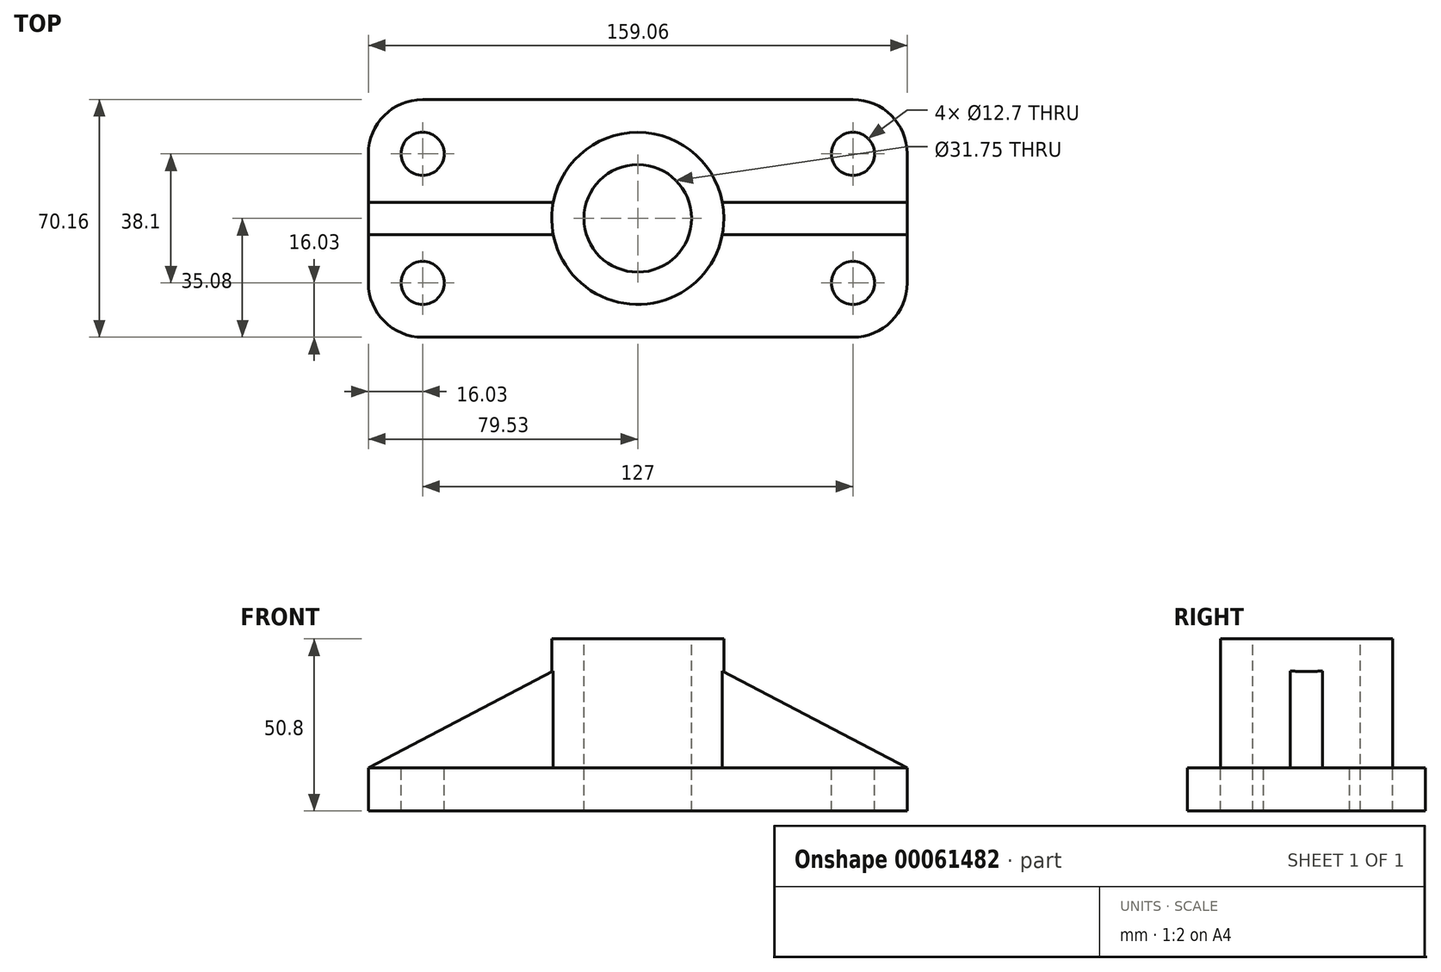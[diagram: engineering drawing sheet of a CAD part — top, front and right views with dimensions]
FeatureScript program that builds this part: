
annotation { "Feature Type Name" : "Feature", "Feature Type Description" : "" }
export const myFeature = defineFeature(function(context is Context, id is Id, definition is map)
    precondition{}
    {
        {
            var Q0;
            Q0=qCreatedBy(makeId("Top.planeOp"),FACE);
            var sketch = newSketch(context, id + "F0", { "sketchPlane" : qUnion([Q0])});
            skLineSegment(sketch, "E0", {"start": v(0, 19.05) * mm, "end": v(0, 0) * mm, "construction": true});
            skLineSegment(sketch, "E1", {"start": v(0, 0) * mm, "end": v(63.5, 0) * mm, "construction": true});
            skLineSegment(sketch, "E2", {"start": v(63.5, 0) * mm, "end": v(63.5, 19.05) * mm, "construction": true});
            skCircle(sketch, "E3", {"center": v(63.5, 19.05) * mm, "radius": 6.35 * mm});
            skCircle(sketch, "E4.MirrorC", {"center": v(63.5, -19.05) * mm, "radius": 6.35 * mm});
            skCircle(sketch, "E5.MirrorC", {"center": v(-63.5, 19.05) * mm, "radius": 6.35 * mm});
            skCircle(sketch, "E6.MirrorC", {"center": v(-63.5, -19.05) * mm, "radius": 6.35 * mm});
            skLineSegment(sketch, "E7", {"start": v(0, -35.08) * mm, "end": v(63.5, -35.08) * mm});
            skLineSegment(sketch, "E8", {"start": v(79.53, 0) * mm, "end": v(79.53, -19.05) * mm});
            skArc(sketch, "E9", {"start": v(63.5, -35.08) * mm, "mid": v(74.83, -30.38) * mm, "end": v(79.53, -19.05) * mm});
            skLineSegment(sketch, "E10.MirrorCS", {"start": v(79.53, 0) * mm, "end": v(79.53, 19.05) * mm});
            skArc(sketch, "E11.MirrorCS", {"start": v(63.5, 35.08) * mm, "mid": v(74.83, 30.38) * mm, "end": v(79.53, 19.05) * mm});
            skLineSegment(sketch, "E12.MirrorCS", {"start": v(0, 35.08) * mm, "end": v(63.5, 35.08) * mm});
            skLineSegment(sketch, "E13.MirrorCS", {"start": v(0, 35.08) * mm, "end": v(-63.5, 35.08) * mm});
            skArc(sketch, "E14.MirrorCS", {"start": v(-63.5, 35.08) * mm, "mid": v(-74.83, 30.38) * mm, "end": v(-79.53, 19.05) * mm});
            skLineSegment(sketch, "E15.MirrorCS", {"start": v(-79.53, 0) * mm, "end": v(-79.53, 19.05) * mm});
            skLineSegment(sketch, "E16.MirrorCS", {"start": v(-79.53, 0) * mm, "end": v(-79.53, -19.05) * mm});
            skArc(sketch, "E17.MirrorCS", {"start": v(-63.5, -35.08) * mm, "mid": v(-74.83, -30.38) * mm, "end": v(-79.53, -19.05) * mm});
            skLineSegment(sketch, "E18.MirrorCS", {"start": v(0, -35.08) * mm, "end": v(-63.5, -35.08) * mm});
            skSolve(sketch);
        }
        {
            var Q0;
            Q0=makeQuery(id+"F0.imprint","IMPRINT",FACE,{"disambiguationData":[TD([[makeQuery(id+"F0.imprint","IMPRINT",EDGE,{"derivedFrom":sQuery(id+"F0.wireOp",EDGE,"E3")}),-1.0]])]});
            extrude(context, id + "F1", {"entities" : qUnion([Q0]), "oppositeDirection" : true, "depth" : 12.7 * mm});
        }
        {
            var Q0;
            Q0=makeQuery(id+"F1.opExtrude","CAP_FACE",FACE,{"disambiguationData":[OSD([sQuery(id+"F0.wireOp",EDGE,"E3"),sQuery(id+"F0.wireOp",EDGE,"E4.MirrorC"),sQuery(id+"F0.wireOp",EDGE,"E5.MirrorC"),sQuery(id+"F0.wireOp",EDGE,"E6.MirrorC"),sQuery(id+"F0.wireOp",EDGE,"E7"),sQuery(id+"F0.wireOp",EDGE,"E8"),sQuery(id+"F0.wireOp",EDGE,"E9"),sQuery(id+"F0.wireOp",EDGE,"E10.MirrorCS"),sQuery(id+"F0.wireOp",EDGE,"E11.MirrorCS"),sQuery(id+"F0.wireOp",EDGE,"E12.MirrorCS"),sQuery(id+"F0.wireOp",EDGE,"E13.MirrorCS"),sQuery(id+"F0.wireOp",EDGE,"E14.MirrorCS"),sQuery(id+"F0.wireOp",EDGE,"E15.MirrorCS"),sQuery(id+"F0.wireOp",EDGE,"E16.MirrorCS"),sQuery(id+"F0.wireOp",EDGE,"E17.MirrorCS"),sQuery(id+"F0.wireOp",EDGE,"E18.MirrorCS")])],"isStart":true});
            var sketch = newSketch(context, id + "F2", { "sketchPlane" : qUnion([Q0])});
            skCircle(sketch, "E19", {"center": v(0, 0) * mm, "radius": 25.4 * mm});
            skSolve(sketch);
        }
        {
            var Q0;
            Q0 = qSketchRegion(id + "F2", true);
            extrude(context, id + "F3", {"entities" : qUnion([Q0]), "operationType" : NewBodyOperationType.ADD, "depth" : 38.1 * mm});
        }
        {
            var Q0;
            Q0=qCreatedBy(makeId("Front.planeOp"),FACE);
            var sketch = newSketch(context, id + "F4", { "sketchPlane" : qUnion([Q0])});
            skLineSegment(sketch, "E20", {"start": v(-79.53, 0) * mm, "end": v(79.53, 0) * mm});
            skLineSegment(sketch, "E21", {"start": v(79.53, 0) * mm, "end": v(19.05, 31.75) * mm});
            skLineSegment(sketch, "E22", {"start": v(19.05, 31.75) * mm, "end": v(-19.05, 31.75) * mm});
            skLineSegment(sketch, "E23", {"start": v(-19.05, 31.75) * mm, "end": v(-79.53, 0) * mm});
            skLineSegment(sketch, "E24", {"start": v(0, 0) * mm, "end": v(0, 31.75) * mm, "construction": true});
            skSolve(sketch);
        }
        {
            var Q0;
            Q0 = qSketchRegion(id + "F4", true);
            extrude(context, id + "F5", {"entities" : qUnion([Q0]), "operationType" : NewBodyOperationType.ADD, "endBound" : BoundingType.SYMMETRIC, "depth" : 9.52 * mm});
        }
        {
            var Q0;
            Q0=makeQuery(id+"F3.opExtrude","CAP_FACE",FACE,{"disambiguationData":[OSD([sQuery(id+"F2.wireOp",EDGE,"E19")])],"isStart":false});
            var sketch = newSketch(context, id + "F6", { "sketchPlane" : qUnion([Q0])});
            skCircle(sketch, "E25", {"center": v(0, 0) * mm, "radius": 15.88 * mm});
            skSolve(sketch);
        }
        {
            var Q0;
            Q0 = qSketchRegion(id + "F6", true);
            extrude(context, id + "F7", {"entities" : qUnion([Q0]), "operationType" : NewBodyOperationType.REMOVE, "endBound" : BoundingType.THROUGH_ALL, "oppositeDirection" : true, "depth" : 25.4 * mm});
        }
    });
